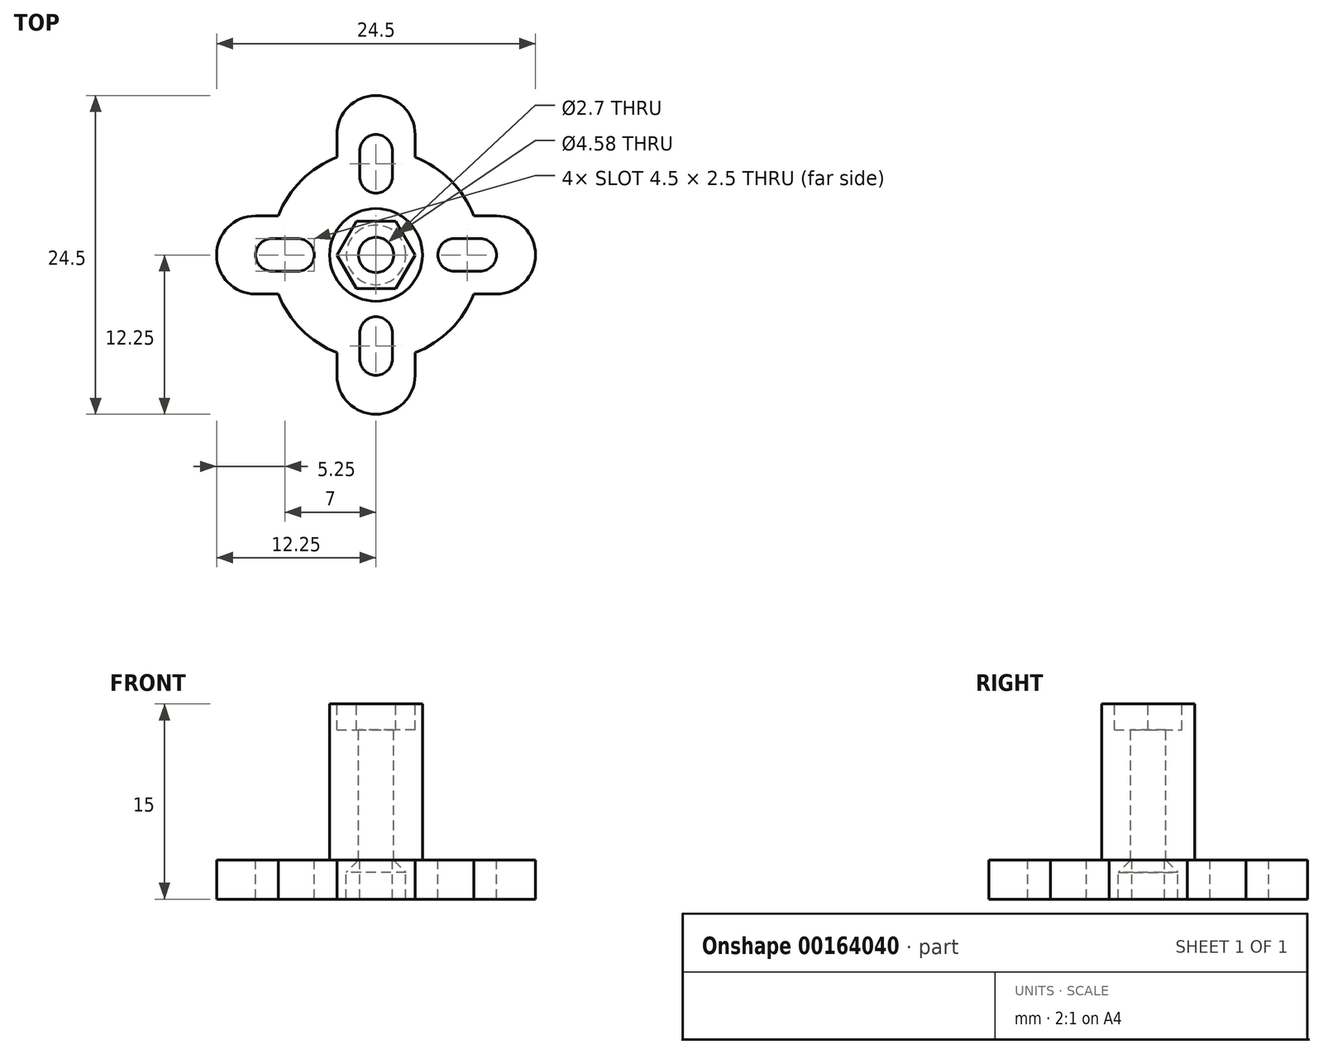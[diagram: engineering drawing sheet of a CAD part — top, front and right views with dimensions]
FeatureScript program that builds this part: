
annotation { "Feature Type Name" : "Feature", "Feature Type Description" : "" }
export const myFeature = defineFeature(function(context is Context, id is Id, definition is map)
    precondition{}
    {
        {
            var Q0;
            Q0=qCreatedBy(makeId("Top.planeOp"),FACE);
            var sketch = newSketch(context, id + "F0", { "sketchPlane" : qUnion([Q0])});
            skCircle(sketch, "E0", {"center": v(0, 0) * mm, "radius": 3.56 * mm, "construction": true});
            skCircle(sketch, "E1", {"center": v(0, 0) * mm, "radius": 8 * mm, "construction": true});
            skCircle(sketch, "E2", {"center": v(0, 0) * mm, "radius": 6 * mm, "construction": true});
            skCircle(sketch, "E3", {"center": v(0, 0) * mm, "radius": 11.5 * mm, "construction": true});
            skLineSegment(sketch, "E4", {"start": v(-8, 0) * mm, "end": v(-6, 0) * mm, "construction": true});
            skArc(sketch, "E5.0.startCap", {"start": v(-8, -1.25) * mm, "mid": v(-9.25, 0) * mm, "end": v(-8, 1.25) * mm, "construction": true});
            skArc(sketch, "E5.0.endCap", {"start": v(-6, 1.25) * mm, "mid": v(-4.75, 0) * mm, "end": v(-6, -1.25) * mm, "construction": true});
            skLineSegment(sketch, "E5.0.left", {"start": v(-8, 1.25) * mm, "end": v(-6, 1.25) * mm, "construction": true});
            skLineSegment(sketch, "E5.0.right", {"start": v(-8, -1.25) * mm, "end": v(-6, -1.25) * mm, "construction": true});
            skArc(sketch, "E6.1.0", {"start": v(1.25, -8) * mm, "mid": v(0, -9.25) * mm, "end": v(-1.25, -8) * mm, "construction": true});
            skLineSegment(sketch, "E6.1.1", {"start": v(-1.25, -8) * mm, "end": v(-1.25, -6) * mm, "construction": true});
            skLineSegment(sketch, "E6.1.2", {"start": v(1.25, -8) * mm, "end": v(1.25, -6) * mm, "construction": true});
            skArc(sketch, "E6.1.3", {"start": v(-1.25, -6) * mm, "mid": v(0, -4.75) * mm, "end": v(1.25, -6) * mm, "construction": true});
            skArc(sketch, "E6.2.0", {"start": v(8, 1.25) * mm, "mid": v(9.25, 0) * mm, "end": v(8, -1.25) * mm, "construction": true});
            skLineSegment(sketch, "E6.2.1", {"start": v(8, -1.25) * mm, "end": v(6, -1.25) * mm, "construction": true});
            skLineSegment(sketch, "E6.2.2", {"start": v(8, 1.25) * mm, "end": v(6, 1.25) * mm, "construction": true});
            skArc(sketch, "E6.2.3", {"start": v(6, -1.25) * mm, "mid": v(4.75, 0) * mm, "end": v(6, 1.25) * mm, "construction": true});
            skArc(sketch, "E6.3.0", {"start": v(-1.25, 8) * mm, "mid": v(0, 9.25) * mm, "end": v(1.25, 8) * mm, "construction": true});
            skLineSegment(sketch, "E6.3.1", {"start": v(1.25, 8) * mm, "end": v(1.25, 6) * mm, "construction": true});
            skLineSegment(sketch, "E6.3.2", {"start": v(-1.25, 8) * mm, "end": v(-1.25, 6) * mm, "construction": true});
            skArc(sketch, "E6.3.3", {"start": v(1.25, 6) * mm, "mid": v(0, 4.75) * mm, "end": v(-1.25, 6) * mm, "construction": true});
            skLineSegment(sketch, "E7", {"start": v(-9.25, 0) * mm, "end": v(-4.75, 0) * mm, "construction": true});
            skArc(sketch, "E8.0.startCap", {"start": v(-9.25, -3) * mm, "mid": v(-12.25, 0) * mm, "end": v(-9.25, 3) * mm, "construction": true});
            skArc(sketch, "E8.0.endCap", {"start": v(-4.75, 3) * mm, "mid": v(-1.75, 0) * mm, "end": v(-4.75, -3) * mm, "construction": true});
            skLineSegment(sketch, "E8.0.left", {"start": v(-9.25, 3) * mm, "end": v(-4.75, 3) * mm, "construction": true});
            skLineSegment(sketch, "E8.0.right", {"start": v(-9.25, -3) * mm, "end": v(-4.75, -3) * mm, "construction": true});
            skArc(sketch, "E9.1.0", {"start": v(3, -9.25) * mm, "mid": v(0, -12.25) * mm, "end": v(-3, -9.25) * mm, "construction": true});
            skLineSegment(sketch, "E9.1.1", {"start": v(-3, -9.25) * mm, "end": v(-3, -4.75) * mm, "construction": true});
            skLineSegment(sketch, "E9.1.2", {"start": v(3, -9.25) * mm, "end": v(3, -4.75) * mm, "construction": true});
            skArc(sketch, "E9.1.3", {"start": v(-3, -4.75) * mm, "mid": v(0, -1.75) * mm, "end": v(3, -4.75) * mm, "construction": true});
            skArc(sketch, "E9.2.0", {"start": v(9.25, 3) * mm, "mid": v(12.25, 0) * mm, "end": v(9.25, -3) * mm, "construction": true});
            skLineSegment(sketch, "E9.2.1", {"start": v(9.25, -3) * mm, "end": v(4.75, -3) * mm, "construction": true});
            skLineSegment(sketch, "E9.2.2", {"start": v(9.25, 3) * mm, "end": v(4.75, 3) * mm, "construction": true});
            skArc(sketch, "E9.2.3", {"start": v(4.75, -3) * mm, "mid": v(1.75, 0) * mm, "end": v(4.75, 3) * mm, "construction": true});
            skArc(sketch, "E9.3.0", {"start": v(-3, 9.25) * mm, "mid": v(0, 12.25) * mm, "end": v(3, 9.25) * mm, "construction": true});
            skLineSegment(sketch, "E9.3.1", {"start": v(3, 9.25) * mm, "end": v(3, 4.75) * mm, "construction": true});
            skLineSegment(sketch, "E9.3.2", {"start": v(-3, 9.25) * mm, "end": v(-3, 4.75) * mm, "construction": true});
            skArc(sketch, "E9.3.3", {"start": v(3, 4.75) * mm, "mid": v(0, 1.75) * mm, "end": v(-3, 4.75) * mm, "construction": true});
            skSolve(sketch);
        }
        {
            var Q0;
            Q0=qCreatedBy(makeId("Top.planeOp"),FACE);
            var sketch = newSketch(context, id + "F1", { "sketchPlane" : qUnion([Q0])});
            skCircle(sketch, "E10.0", {"center": v(0, 0) * mm, "radius": 3.56 * mm});
            skSolve(sketch);
        }
        {
            var Q0;
            Q0=qCreatedBy(makeId("Top.planeOp"),FACE);
            var sketch = newSketch(context, id + "F2", { "sketchPlane" : qUnion([Q0])});
            skArc(sketch, "E11.0", {"start": v(-8, -1.25) * mm, "mid": v(-9.25, 0) * mm, "end": v(-8, 1.25) * mm});
            skArc(sketch, "E12.0", {"start": v(-1.25, -6) * mm, "mid": v(0, -4.75) * mm, "end": v(1.25, -6) * mm});
            skArc(sketch, "E13.0", {"start": v(6, -1.25) * mm, "mid": v(4.75, 0) * mm, "end": v(6, 1.25) * mm});
            skArc(sketch, "E14.0", {"start": v(8, 1.25) * mm, "mid": v(9.25, 0) * mm, "end": v(8, -1.25) * mm});
            skArc(sketch, "E15.0", {"start": v(1.25, 6) * mm, "mid": v(0, 4.75) * mm, "end": v(-1.25, 6) * mm});
            skArc(sketch, "E16.0", {"start": v(1.25, -8) * mm, "mid": v(0, -9.25) * mm, "end": v(-1.25, -8) * mm});
            skArc(sketch, "E17.0", {"start": v(-6, 1.25) * mm, "mid": v(-4.75, 0) * mm, "end": v(-6, -1.25) * mm});
            skArc(sketch, "E18.0", {"start": v(-1.25, 8) * mm, "mid": v(0, 9.25) * mm, "end": v(1.25, 8) * mm});
            skLineSegment(sketch, "E19.0", {"start": v(-8, 1.25) * mm, "end": v(-6, 1.25) * mm});
            skLineSegment(sketch, "E20.0", {"start": v(-8, -1.25) * mm, "end": v(-6, -1.25) * mm});
            skLineSegment(sketch, "E21.0", {"start": v(-1.25, -8) * mm, "end": v(-1.25, -6) * mm});
            skLineSegment(sketch, "E22.0", {"start": v(1.25, -8) * mm, "end": v(1.25, -6) * mm});
            skLineSegment(sketch, "E23.0", {"start": v(8, -1.25) * mm, "end": v(6, -1.25) * mm});
            skLineSegment(sketch, "E24.0", {"start": v(8, 1.25) * mm, "end": v(6, 1.25) * mm});
            skLineSegment(sketch, "E25.0", {"start": v(1.25, 8) * mm, "end": v(1.25, 6) * mm});
            skLineSegment(sketch, "E26.0", {"start": v(-1.25, 8) * mm, "end": v(-1.25, 6) * mm});
            skArc(sketch, "E27.0", {"start": v(-9.25, -3) * mm, "mid": v(-12.25, 0) * mm, "end": v(-9.25, 3) * mm});
            skArc(sketch, "E28.0", {"start": v(3, -9.25) * mm, "mid": v(0, -12.25) * mm, "end": v(-3, -9.25) * mm});
            skArc(sketch, "E29.0", {"start": v(9.25, 3) * mm, "mid": v(12.25, 0) * mm, "end": v(9.25, -3) * mm});
            skArc(sketch, "E30.0", {"start": v(-3, 9.25) * mm, "mid": v(0, 12.25) * mm, "end": v(3, 9.25) * mm});
            skLineSegment(sketch, "E31.0", {"start": v(-9.25, 3) * mm, "end": v(-4.75, 3) * mm});
            skLineSegment(sketch, "E32.0", {"start": v(-9.25, -3) * mm, "end": v(-4.75, -3) * mm});
            skLineSegment(sketch, "E33.0", {"start": v(-3, -9.25) * mm, "end": v(-3, -4.75) * mm});
            skLineSegment(sketch, "E34.0", {"start": v(3, -9.25) * mm, "end": v(3, -4.75) * mm});
            skLineSegment(sketch, "E35.0", {"start": v(9.25, -3) * mm, "end": v(4.75, -3) * mm});
            skLineSegment(sketch, "E36.0", {"start": v(9.25, 3) * mm, "end": v(4.75, 3) * mm});
            skLineSegment(sketch, "E37.0", {"start": v(3, 9.25) * mm, "end": v(3, 4.75) * mm});
            skLineSegment(sketch, "E38.0", {"start": v(-3, 9.25) * mm, "end": v(-3, 4.75) * mm});
            skArc(sketch, "E39", {"start": v(-8, 1.25) * mm, "mid": v(-5.73, 5.73) * mm, "end": v(-1.25, 8) * mm});
            skArc(sketch, "E40", {"start": v(-8, -1.25) * mm, "mid": v(-5.73, -5.73) * mm, "end": v(-1.25, -8) * mm});
            skArc(sketch, "E41", {"start": v(1.25, -8) * mm, "mid": v(5.73, -5.73) * mm, "end": v(8, -1.25) * mm});
            skArc(sketch, "E42", {"start": v(1.25, 8) * mm, "mid": v(5.73, 5.73) * mm, "end": v(8, 1.25) * mm});
            skSolve(sketch);
        }
        {
            var Q0;
            Q0=makeQuery(id+"F1.imprint","IMPRINT",FACE,{"disambiguationData":[TD([[makeQuery(id+"F1.imprint","IMPRINT",EDGE,{"derivedFrom":sQuery(id+"F1.wireOp",EDGE,"E10.0")}),1.0]])]});
            extrude(context, id + "F3", {"entities" : qUnion([Q0]), "depth" : 12 * mm});
        }
        {
            var Q0;
            Q0=makeQuery(id+"F3.opExtrude","CAP_FACE",FACE,{"disambiguationData":[OSD([sQuery(id+"F1.wireOp",EDGE,"E10.0")])],"isStart":false});
            var sketch = newSketch(context, id + "F4", { "sketchPlane" : qUnion([Q0])});
            skCircle(sketch, "E43.cCircle", {"center": v(0, 0) * mm, "radius": 2.6 * mm, "construction": true});
            skLineSegment(sketch, "E43.0", {"start": v(-1.5, 2.6) * mm, "end": v(1.5, 2.6) * mm});
            skLineSegment(sketch, "E43.1", {"start": v(1.5, 2.6) * mm, "end": v(3, 0) * mm});
            skLineSegment(sketch, "E43.2", {"start": v(3, 0) * mm, "end": v(1.5, -2.6) * mm});
            skLineSegment(sketch, "E43.3", {"start": v(1.5, -2.6) * mm, "end": v(-1.5, -2.6) * mm});
            skLineSegment(sketch, "E43.4", {"start": v(-1.5, -2.6) * mm, "end": v(-3, 0) * mm});
            skLineSegment(sketch, "E43.5", {"start": v(-3, 0) * mm, "end": v(-1.5, 2.6) * mm});
            skPoint(sketch, "E43.0.midPoint", {"position": v(0, 2.6) * mm});
            skSolve(sketch);
        }
        {
            var Q0;
            Q0 = qSketchRegion(id + "F2", true);
            extrude(context, id + "F5", {"entities" : qUnion([Q0]), "operationType" : NewBodyOperationType.ADD, "oppositeDirection" : true, "depth" : 3 * mm});
        }
        {
            var Q0;
            Q0=qCreatedBy(makeId("Front.planeOp"),FACE);
            var sketch = newSketch(context, id + "F6", { "sketchPlane" : qUnion([Q0])});
            skLineSegment(sketch, "E44.bottom", {"start": v(0, 0) * mm, "end": v(-1.35, 0) * mm});
            skLineSegment(sketch, "E44.top", {"start": v(0, 17.7) * mm, "end": v(-1.35, 17.7) * mm});
            skLineSegment(sketch, "E44.left", {"start": v(0, 0) * mm, "end": v(0, 17.7) * mm});
            skLineSegment(sketch, "E44.right", {"start": v(-1.35, 0) * mm, "end": v(-1.35, 17.7) * mm});
            skLineSegment(sketch, "E45", {"start": v(0, 1.35) * mm, "end": v(-2.29, -0.94) * mm});
            skLineSegment(sketch, "E46", {"start": v(-2.29, -0.94) * mm, "end": v(0, -0.94) * mm});
            skLineSegment(sketch, "E47", {"start": v(0, -0.94) * mm, "end": v(0, 0) * mm});
            skLineSegment(sketch, "E48.top", {"start": v(-2.29, -4.38) * mm, "end": v(0, -4.38) * mm});
            skLineSegment(sketch, "E48.left", {"start": v(-2.29, -0.94) * mm, "end": v(-2.29, -4.38) * mm});
            skLineSegment(sketch, "E48.right", {"start": v(0, -0.94) * mm, "end": v(0, -4.38) * mm});
            skSolve(sketch);
        }
        {
            var Q0;
            Q0 = qSketchRegion(id + "F6", true);
            var Q1;
            Q1=sQuery(id+"F6.wireOp",EDGE,"E44.left");
            revolve(context, id + "F7", {"operationType" : NewBodyOperationType.REMOVE, "entities" : qUnion([Q0]), "axis" : qUnion([Q1]), "revolveType" : RevolveType.FULL, "oppositeDirection" : true});
        }
        {
            var Q0;
            Q0 = qSketchRegion(id + "F4", true);
            extrude(context, id + "F8", {"entities" : qUnion([Q0]), "operationType" : NewBodyOperationType.REMOVE, "oppositeDirection" : true, "depth" : 2 * mm});
        }
    });
